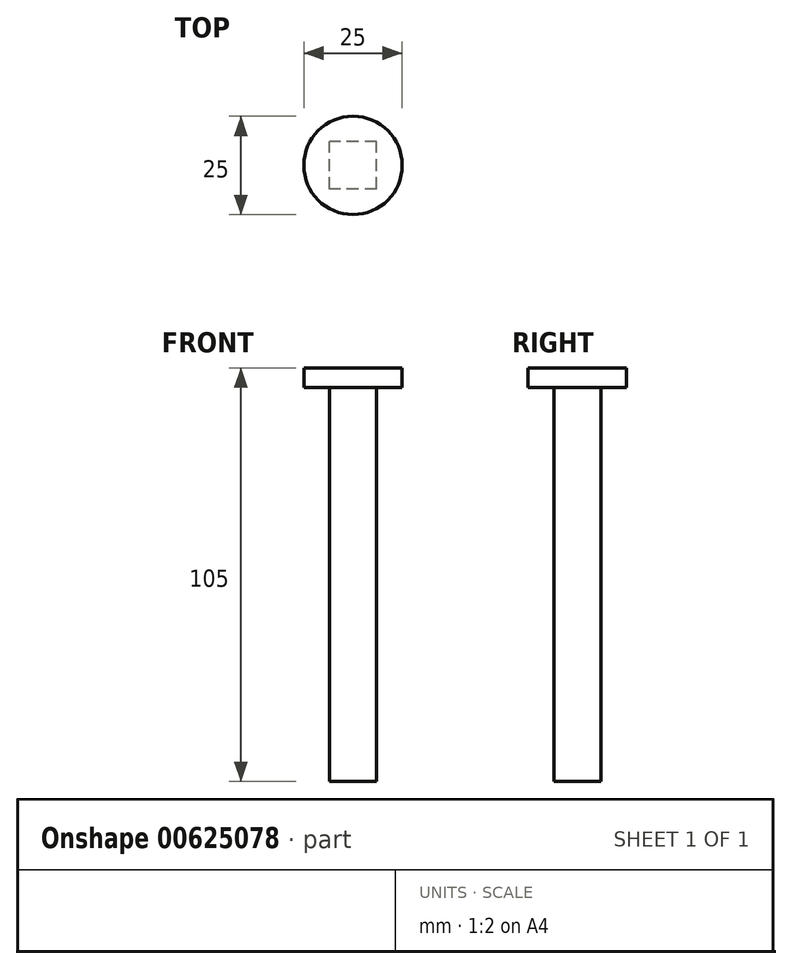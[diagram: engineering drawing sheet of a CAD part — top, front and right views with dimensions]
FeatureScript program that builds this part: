
annotation { "Feature Type Name" : "Feature", "Feature Type Description" : "" }
export const myFeature = defineFeature(function(context is Context, id is Id, definition is map)
    precondition{}
    {
        {
            var Q0;
            Q0=qCreatedBy(makeId("Top.planeOp"),FACE);
            var sketch = newSketch(context, id + "F0", { "sketchPlane" : qUnion([Q0])});
            skLineSegment(sketch, "E0.bottom", {"start": v(6, -6) * mm, "end": v(-6, -6) * mm});
            skLineSegment(sketch, "E0.top", {"start": v(6, 6) * mm, "end": v(-6, 6) * mm});
            skLineSegment(sketch, "E0.left", {"start": v(6, -6) * mm, "end": v(6, 6) * mm});
            skLineSegment(sketch, "E0.right", {"start": v(-6, -6) * mm, "end": v(-6, 6) * mm});
            skPoint(sketch, "E0.middle", {"position": v(0, 0) * mm});
            skSolve(sketch);
        }
        {
            var Q0;
            Q0=makeQuery(id+"F0.imprint","IMPRINT",FACE,{"disambiguationData":[TD([[makeQuery(id+"F0.imprint","IMPRINT",EDGE,{"derivedFrom":sQuery(id+"F0.wireOp",EDGE,"E0.bottom")}),-1.0]])]});
            extrude(context, id + "F1", {"entities" : qUnion([Q0]), "depth" : 100 * mm, "offsetDistance" : 25 * mm});
        }
        {
            var Q0;
            Q0=qCreatedBy(makeId("Top.planeOp"),FACE);
            cPlane(context, id + "F2", {"entities" : qUnion([Q0]), "cplaneType" : CPlaneType.OFFSET, "offset" : 100 * mm, "width" : 150 * mm, "height" : 150 * mm});
        }
        {
            var Q0;
            Q0=qCreatedBy(id+"F2.planeOp",FACE);
            var sketch = newSketch(context, id + "F3", { "sketchPlane" : qUnion([Q0])});
            skCircle(sketch, "E1", {"center": v(0, 0) * mm, "radius": 12.5 * mm});
            skSolve(sketch);
        }
        {
            var Q0;
            Q0=makeQuery(id+"F3.imprint","IMPRINT",FACE,{"disambiguationData":[TD([[makeQuery(id+"F3.imprint","IMPRINT",EDGE,{"derivedFrom":sQuery(id+"F3.wireOp",EDGE,"E1")}),1.0]])]});
            extrude(context, id + "F4", {"entities" : qUnion([Q0]), "operationType" : NewBodyOperationType.ADD, "depth" : 5 * mm, "offsetDistance" : 25 * mm});
        }
    });
